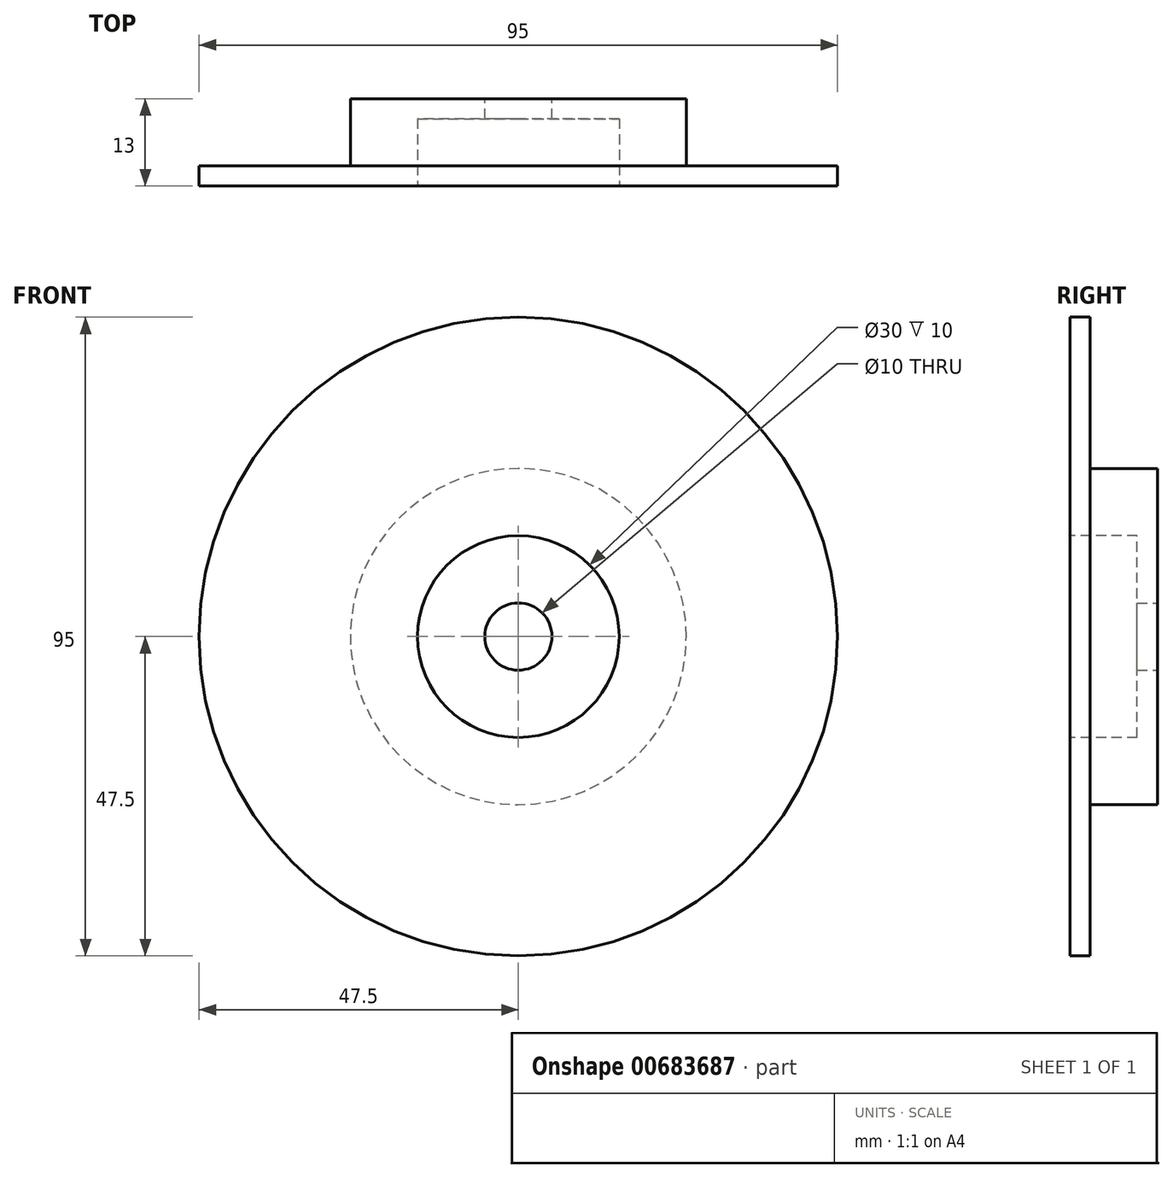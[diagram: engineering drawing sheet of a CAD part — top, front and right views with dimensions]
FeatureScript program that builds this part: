
annotation { "Feature Type Name" : "Feature", "Feature Type Description" : "" }
export const myFeature = defineFeature(function(context is Context, id is Id, definition is map)
    precondition{}
    {
        {
            var Q0;
            Q0=qCreatedBy(makeId("Front.planeOp"),FACE);
            var sketch = newSketch(context, id + "F0", { "sketchPlane" : qUnion([Q0])});
            skCircle(sketch, "E0", {"center": v(0, 0) * mm, "radius": 47.5 * mm});
            skSolve(sketch);
        }
        {
            var Q0;
            Q0 = qSketchRegion(id + "F0", true);
            extrude(context, id + "F1", {"entities" : qUnion([Q0]), "depth" : 13 * mm, "offsetDistance" : 25 * mm});
        }
        {
            var Q0;
            Q0=makeQuery(id+"F1.opExtrude","CAP_FACE",FACE,{"disambiguationData":[OSD([sQuery(id+"F0.wireOp",EDGE,"E0")])],"isStart":false});
            var sketch = newSketch(context, id + "F2", { "sketchPlane" : qUnion([Q0])});
            skCircle(sketch, "E1", {"center": v(0, 0) * mm, "radius": 15 * mm});
            skSolve(sketch);
        }
        {
            var Q0;
            Q0 = qSketchRegion(id + "F2", true);
            extrude(context, id + "F3", {"entities" : qUnion([Q0]), "operationType" : NewBodyOperationType.REMOVE, "oppositeDirection" : true, "depth" : 10 * mm, "offsetDistance" : 25 * mm});
        }
        {
            var Q0;
            Q0=makeQuery(id+"F1.opExtrude","CAP_FACE",FACE,{"disambiguationData":[OSD([sQuery(id+"F0.wireOp",EDGE,"E0")])],"isStart":true});
            var sketch = newSketch(context, id + "F4", { "sketchPlane" : qUnion([Q0])});
            skCircle(sketch, "E2", {"center": v(0, 0) * mm, "radius": 25 * mm});
            skCircle(sketch, "E3", {"center": v(0, -4.28) * mm, "radius": 58.55 * mm});
            skSolve(sketch);
        }
        {
            var Q0;
            Q0 = qSketchRegion(id + "F4", true);
            extrude(context, id + "F5", {"entities" : qUnion([Q0]), "operationType" : NewBodyOperationType.REMOVE, "oppositeDirection" : true, "depth" : 10 * mm, "offsetDistance" : 25 * mm});
        }
        {
            var Q0;
            Q0=makeQuery(id+"F1.opExtrude","CAP_FACE",FACE,{"disambiguationData":[OSD([sQuery(id+"F0.wireOp",EDGE,"E0")])],"isStart":true});
            var sketch = newSketch(context, id + "F6", { "sketchPlane" : qUnion([Q0])});
            skCircle(sketch, "E4", {"center": v(0, 0) * mm, "radius": 5 * mm});
            skSolve(sketch);
        }
        {
            var Q0;
            Q0 = qSketchRegion(id + "F6", true);
            extrude(context, id + "F7", {"entities" : qUnion([Q0]), "operationType" : NewBodyOperationType.REMOVE, "oppositeDirection" : true, "depth" : 25 * mm, "offsetDistance" : 25 * mm});
        }
    });
